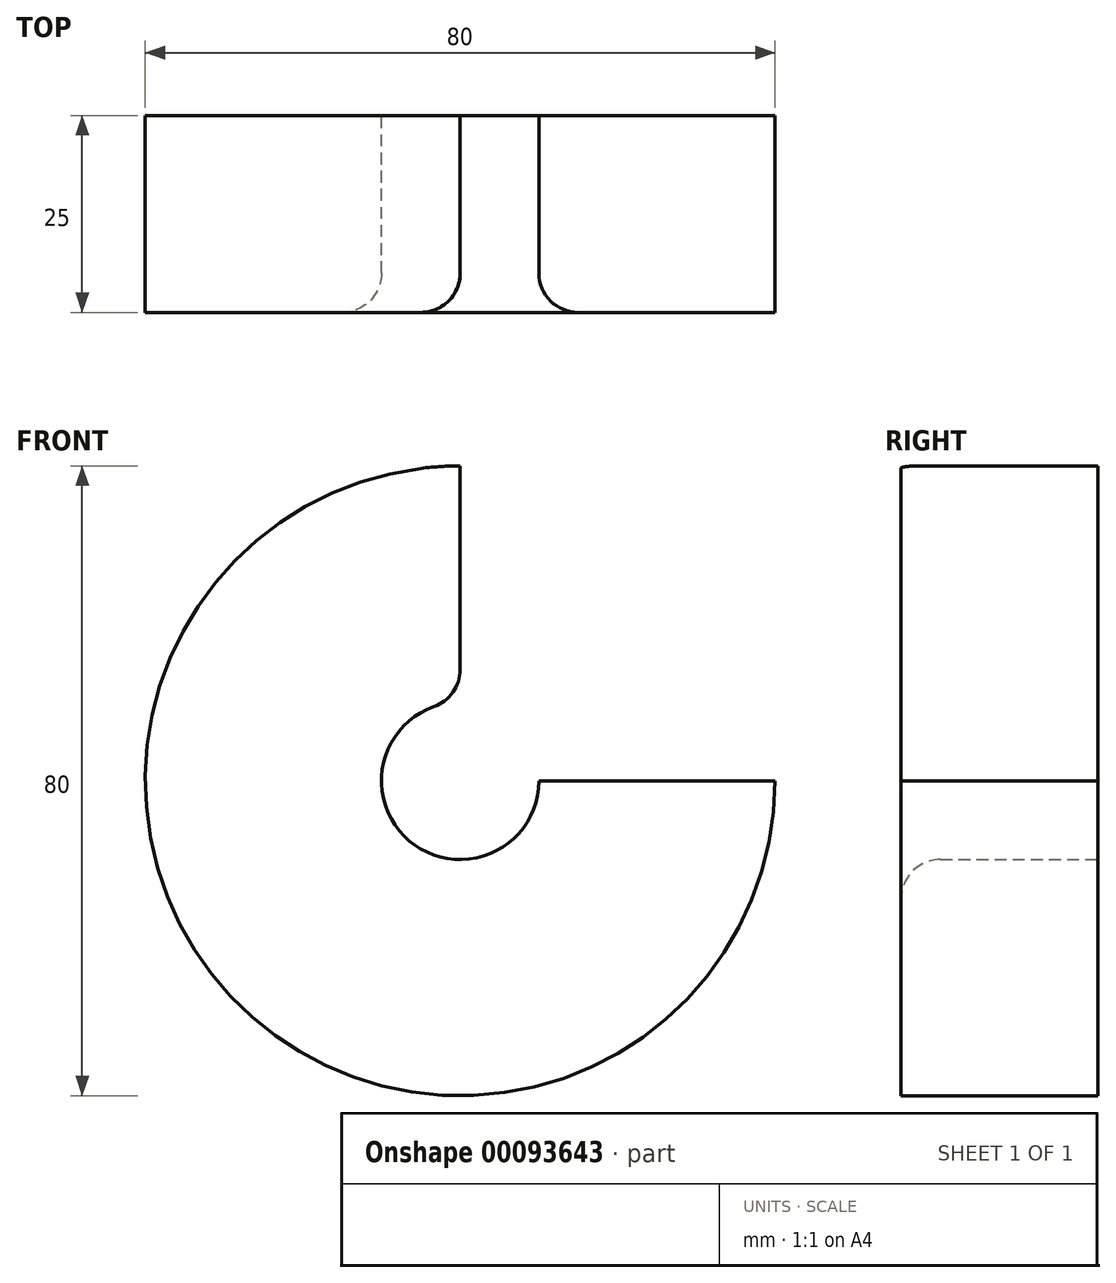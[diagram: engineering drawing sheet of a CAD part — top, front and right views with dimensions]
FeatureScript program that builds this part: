
annotation { "Feature Type Name" : "Feature", "Feature Type Description" : "" }
export const myFeature = defineFeature(function(context is Context, id is Id, definition is map)
    precondition{}
    {
        {
            var Q0;
            Q0=qCreatedBy(makeId("Front.planeOp"),FACE);
            var sketch = newSketch(context, id + "F0", { "sketchPlane" : qUnion([Q0])});
            skArc(sketch, "E0", {"start": v(0, 40) * mm, "mid": v(-28.28, -28.28) * mm, "end": v(40, 0) * mm});
            skArc(sketch, "E1", {"start": v(0, 10) * mm, "mid": v(-7.07, -7.07) * mm, "end": v(10, 0) * mm});
            skLineSegment(sketch, "E2", {"start": v(0, 40) * mm, "end": v(0, 10) * mm});
            skLineSegment(sketch, "E3", {"start": v(40, 0) * mm, "end": v(10, 0) * mm});
            skSolve(sketch);
        }
        {
            var Q0;
            Q0 = qSketchRegion(id + "F0", true);
            extrude(context, id + "F1", {"entities" : qUnion([Q0]), "depth" : 25 * mm});
        }
        {
            var Q0;
            Q0=makeQuery(id+"F1.opExtrude","CAP_EDGE",EDGE,{"disambiguationData":[OSD([sQuery(id+"F0.wireOp",EDGE,"E1")])],"isStart":false});
            var Q1;
            Q1=makeQuery(id+"F1.opExtrude","CAP_EDGE",EDGE,{"disambiguationData":[OSD([sQuery(id+"F0.wireOp",EDGE,"E2")])],"isStart":false});
            var Q2;
            Q2=makeQuery(id+"F1.opExtrude","SWEPT_EDGE",EDGE,{"disambiguationData":[OSD([sQuery(id+"F0.wireOp",EDGE,"E1"),sQuery(id+"F0.wireOp",EDGE,"E2")])]});
            fillet(context, id + "F2", {"entities" : qUnion([Q0, Q1, Q2]), "radius" : 5 * mm, "tangentPropagation" : true, "allowEdgeOverflow" : false});
        }
    });
